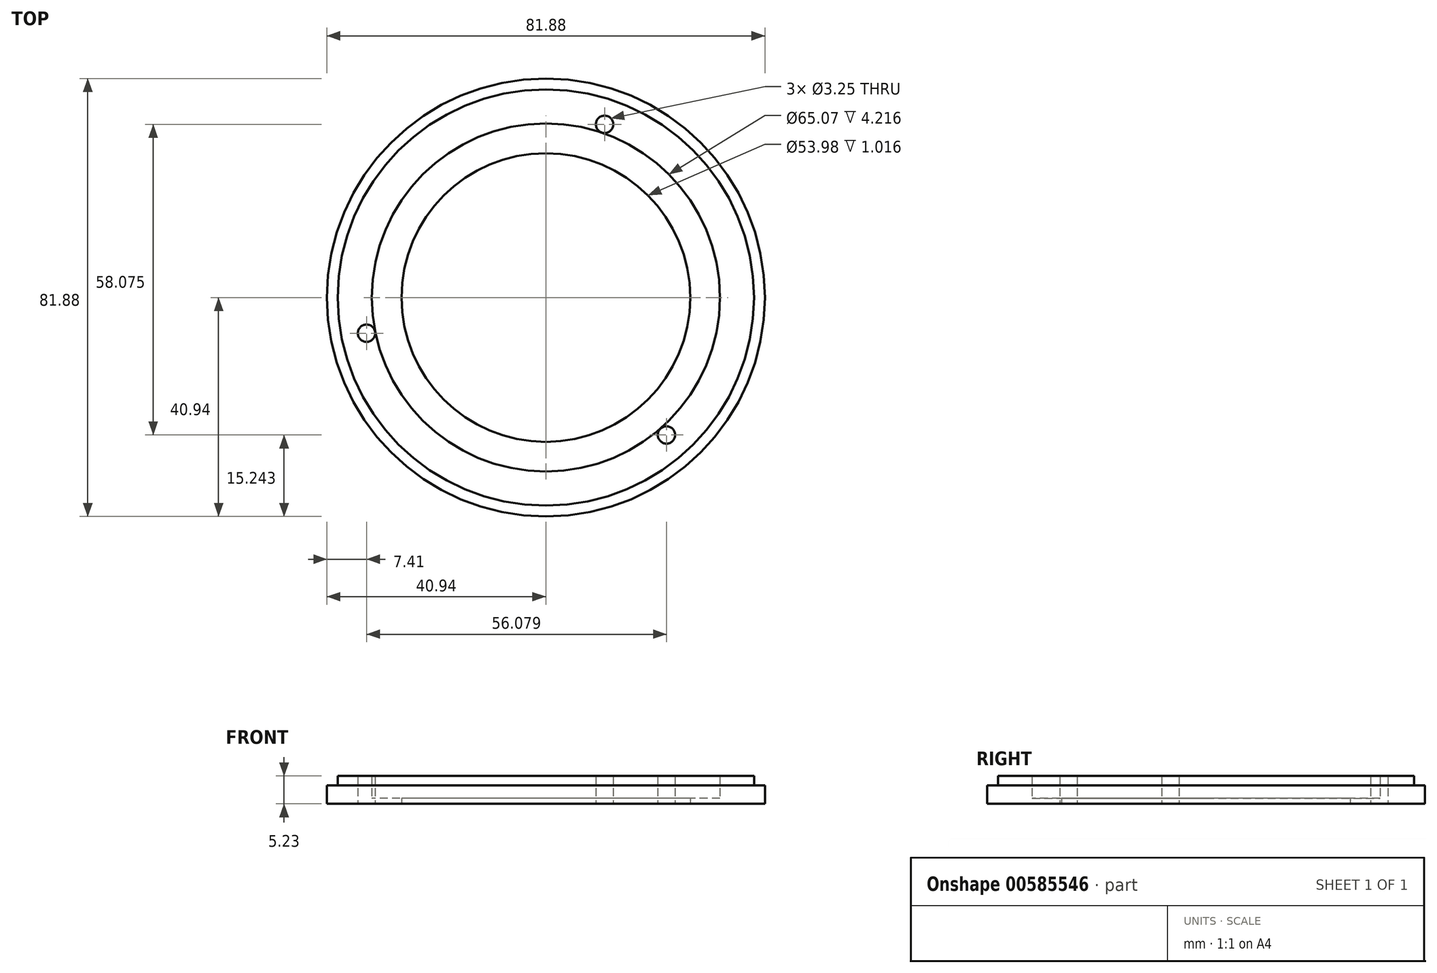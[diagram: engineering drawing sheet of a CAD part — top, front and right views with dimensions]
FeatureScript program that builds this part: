
annotation { "Feature Type Name" : "Feature", "Feature Type Description" : "" }
export const myFeature = defineFeature(function(context is Context, id is Id, definition is map)
    precondition{}
    {
        {
            var Q0;
            Q0=qCreatedBy(makeId("Top.planeOp"),FACE);
            var sketch = newSketch(context, id + "F0", { "sketchPlane" : qUnion([Q0])});
            skCircle(sketch, "E0", {"center": v(0, 0) * mm, "radius": 38.91 * mm});
            skCircle(sketch, "E1", {"center": v(0, 0) * mm, "radius": 40.94 * mm});
            skCircle(sketch, "E2", {"center": v(0, 0) * mm, "radius": 32.54 * mm});
            skCircle(sketch, "E3", {"center": v(0, 0) * mm, "radius": 34.19 * mm, "construction": true});
            skCircle(sketch, "E4", {"center": v(0, 0) * mm, "radius": 26.99 * mm});
            skCircle(sketch, "E5", {"center": v(22.55, -25.7) * mm, "radius": 1.63 * mm});
            skCircle(sketch, "E6.1.0", {"center": v(10.98, 32.38) * mm, "radius": 1.63 * mm});
            skCircle(sketch, "E6.2.0", {"center": v(-33.53, -6.68) * mm, "radius": 1.63 * mm});
            skSolve(sketch);
        }
        {
            var Q0;
            Q0=makeQuery(id+"F0.imprint","IMPRINT",FACE,{"disambiguationData":[TD([[makeQuery(id+"F0.imprint","IMPRINT",EDGE,{"derivedFrom":sQuery(id+"F0.wireOp",EDGE,"E0")}),1.0]])]});
            extrude(context, id + "F1", {"entities" : qUnion([Q0]), "depth" : 5.23 * mm, "offsetDistance" : 25.4 * mm});
        }
        {
            var Q0;
            Q0=qCreatedBy(makeId("Top.planeOp"),FACE);
            var sketch = newSketch(context, id + "F2", { "sketchPlane" : qUnion([Q0])});
            skCircle(sketch, "E7", {"center": v(0, 0) * mm, "radius": 38.91 * mm});
            skCircle(sketch, "E8", {"center": v(0, 0) * mm, "radius": 40.94 * mm});
            skCircle(sketch, "E9", {"center": v(0, 0) * mm, "radius": 32.54 * mm});
            skCircle(sketch, "E10", {"center": v(0, 0) * mm, "radius": 34.19 * mm, "construction": true});
            skCircle(sketch, "E11", {"center": v(0, 0) * mm, "radius": 26.99 * mm});
            skCircle(sketch, "E12", {"center": v(22.55, -25.7) * mm, "radius": 1.63 * mm});
            skCircle(sketch, "E13.1.0", {"center": v(10.98, 32.38) * mm, "radius": 1.63 * mm});
            skCircle(sketch, "E13.2.0", {"center": v(-33.53, -6.68) * mm, "radius": 1.63 * mm});
            skSolve(sketch);
        }
        {
            var Q0;
            Q0=makeQuery(id+"F2.imprint","IMPRINT",FACE,{"disambiguationData":[TD([[makeQuery(id+"F2.imprint","IMPRINT",EDGE,{"derivedFrom":sQuery(id+"F2.wireOp",EDGE,"E9")}),1.0]])]});
            extrude(context, id + "F3", {"entities" : qUnion([Q0]), "operationType" : NewBodyOperationType.ADD, "depth" : 1.02 * mm, "offsetDistance" : 25.4 * mm});
        }
        {
            var Q0;
            Q0=qCreatedBy(makeId("Top.planeOp"),FACE);
            var sketch = newSketch(context, id + "F4", { "sketchPlane" : qUnion([Q0])});
            skCircle(sketch, "E14", {"center": v(0, 0) * mm, "radius": 38.91 * mm});
            skCircle(sketch, "E15", {"center": v(0, 0) * mm, "radius": 40.94 * mm});
            skCircle(sketch, "E16", {"center": v(0, 0) * mm, "radius": 32.54 * mm});
            skCircle(sketch, "E17", {"center": v(0, 0) * mm, "radius": 34.19 * mm, "construction": true});
            skCircle(sketch, "E18", {"center": v(0, 0) * mm, "radius": 26.99 * mm});
            skCircle(sketch, "E19", {"center": v(22.55, -25.7) * mm, "radius": 1.63 * mm});
            skCircle(sketch, "E20.1.0", {"center": v(10.98, 32.38) * mm, "radius": 1.63 * mm});
            skCircle(sketch, "E20.2.0", {"center": v(-33.53, -6.68) * mm, "radius": 1.63 * mm});
            skSolve(sketch);
        }
        {
            var Q0;
            Q0=makeQuery(id+"F4.imprint","IMPRINT",FACE,{"disambiguationData":[TD([[makeQuery(id+"F4.imprint","IMPRINT",EDGE,{"derivedFrom":sQuery(id+"F4.wireOp",EDGE,"E14")}),-1.0]])]});
            extrude(context, id + "F5", {"entities" : qUnion([Q0]), "operationType" : NewBodyOperationType.ADD, "depth" : 3.45 * mm, "offsetDistance" : 25.4 * mm});
        }
    });
